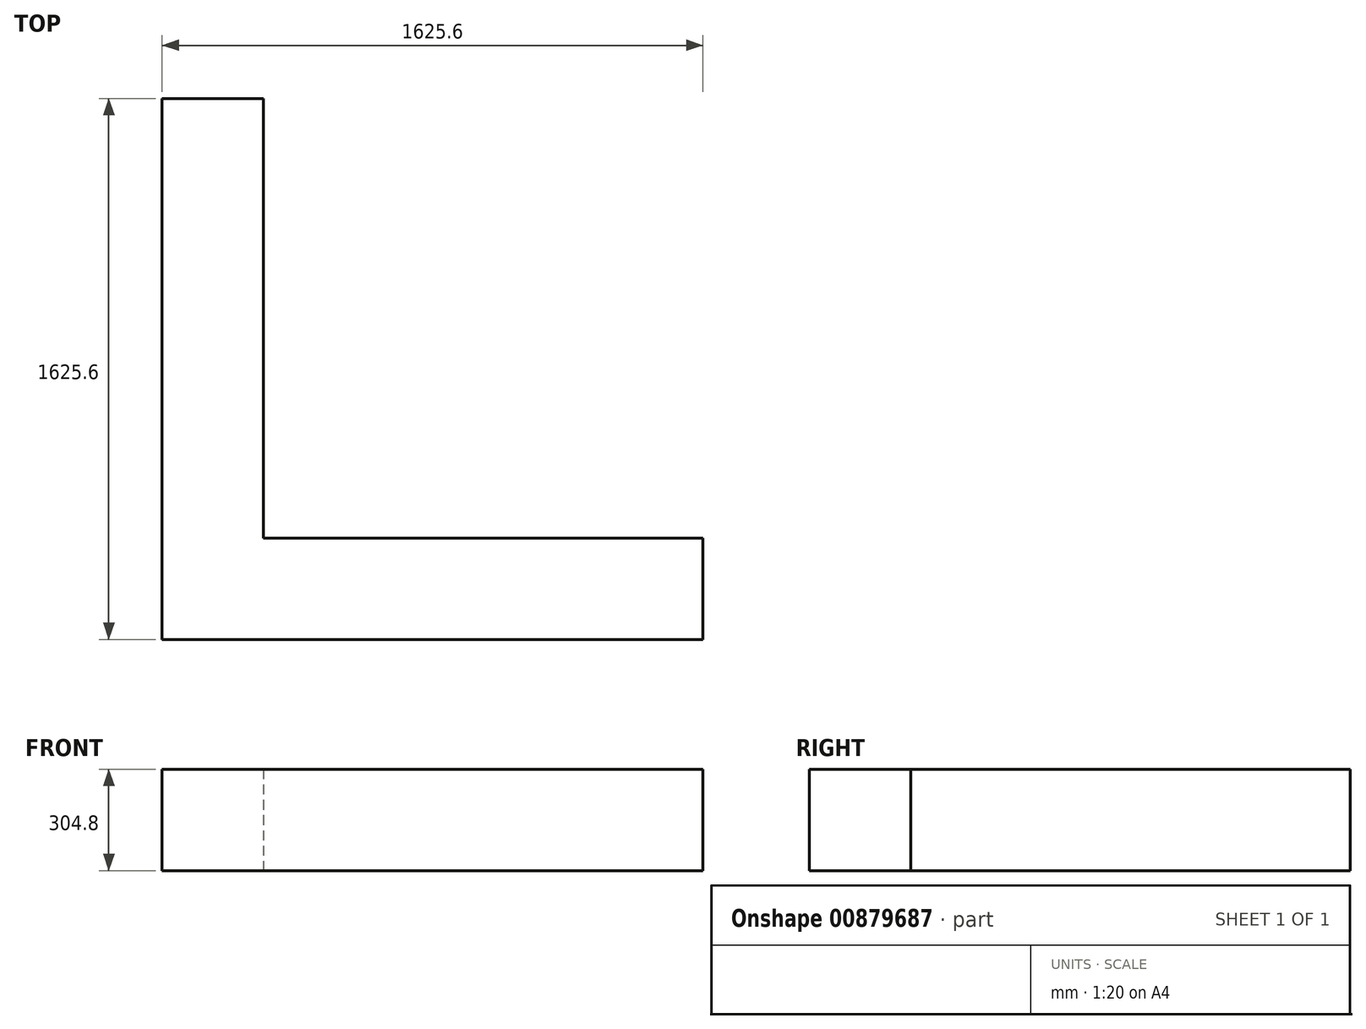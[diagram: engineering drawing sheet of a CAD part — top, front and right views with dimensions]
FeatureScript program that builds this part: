
annotation { "Feature Type Name" : "Feature", "Feature Type Description" : "" }
export const myFeature = defineFeature(function(context is Context, id is Id, definition is map)
    precondition{}
    {
        {
            var Q0;
            Q0=qCreatedBy(makeId("Top.planeOp"),FACE);
            var sketch = newSketch(context, id + "F0", { "sketchPlane" : qUnion([Q0])});
            skLineSegment(sketch, "E0", {"start": v(0, 0) * mm, "end": v(1625.6, 0) * mm});
            skLineSegment(sketch, "E1", {"start": v(1625.6, 0) * mm, "end": v(1625.6, 304.8) * mm});
            skLineSegment(sketch, "E2", {"start": v(1625.6, 304.8) * mm, "end": v(304.8, 304.8) * mm});
            skLineSegment(sketch, "E3", {"start": v(304.8, 304.8) * mm, "end": v(304.8, 1625.6) * mm});
            skLineSegment(sketch, "E4", {"start": v(304.8, 1625.6) * mm, "end": v(0, 1625.6) * mm});
            skLineSegment(sketch, "E5", {"start": v(0, 1625.6) * mm, "end": v(0, 0) * mm});
            skSolve(sketch);
        }
        {
            var Q0;
            Q0=makeQuery(id+"F0.imprint","IMPRINT",FACE,{"disambiguationData":[TD([[makeQuery(id+"F0.imprint","IMPRINT",EDGE,{"derivedFrom":sQuery(id+"F0.wireOp",EDGE,"E0")}),1.0]])]});
            extrude(context, id + "F1", {"entities" : qUnion([Q0]), "depth" : 304.8 * mm, "offsetDistance" : 25.4 * mm});
        }
    });
